# Revit family: DEVIreg Hotwater_1
name_source: partatom
category: Data Devices
units: mm (PartAtom-declared; Revit-internal decimal feet)

## family parameters
Cut with Voids When Loaded = No
Host = Face
Maintain Annotation Orientation = No
OmniClass Number = 23.85.50.17
OmniClass Title = Communication and Data Processing Equipment
Part Type = Normal
Room Calculation Point = No
Round Connector Dimension = Use Diameter
Shared = No

## types (1)
- DEVIreg™ Hotwater_140F1133
    Ball pressure test temperature = 125 °C
    Battery back-up time, min = 48 hours
    Body Material = Danfoss Plastic Dark Gray
    Cable specification max. = 0.2-2.5 mm²
    Communication Protocol = MODBUS
    Controller type = 1C
    D = 63 mm  [stored 0.206693 ft]
    Default Elevation = 0 mm  [stored 0 ft]
    Description = Programmable controller with Wire sensor
    H = 110 mm  [stored 0.360892 ft]
    IP Rating = IP40 only on the front cover
    IfcExportAs = IfcElectricApplianceType
    IfcExportType = DEVIreg Hotwater
    Immunity against voltage surges = Designed for Over Voltage Category II
    Inductive load = 32 A
    L = 63 mm  [stored 0.206693 ft]
    LOD 200 = No
    LOD 350 = Yes
    Manufacturer = Danfoss
    Model = 140F1133
    Model Type = DEVIreg™ Hotwater
    Mounting method = DIN rail, complying with EN 60715
    NominalHeight = 110 mm  [stored 0.360892 ft]
    NominalLength = 63 mm  [stored 0.206693 ft]
    NominalWidth = 138 mm  [stored 0.452756 ft]
    Operating Temperature Range = CE: -20T60 / UL: 0T55, 90% RH non-condensing
    Pollution degree = 2
    Power = 20 W
    Protection class = Class II
    Sensing unit = NTC15k (15 kOhm @ 25 °C) (standard)
NTC10k (10 kOhm @ 25 °C)
NTC5k (5 kOhm @ 25 °C)
NTC2k (2 kOhm @ 25 °C)
NTC100 (100 kOhm @ 25 °C)
NTC16k (16,7 kOhm @ 100 °C)
PT1000 (1000 Ohm @ 0 °C)
    Software class = A
    Storage temperature = 30...+85 °C, 90% RH non-condensing
    URL = https://store.danfoss.com
    Voltage = 230 V
    W = 138 mm  [stored 0.452756 ft]
    Weight = 0.51 kg
    r = 55 mm  [stored 0.180446 ft]

note: [stored X ft] marks values corroborated as IEEE doubles in the binary element streams (Revit-internal decimal feet)

## geometry (parser evidence)
native form markers: Sweep x2
no freeform markers — native parametric forms only
